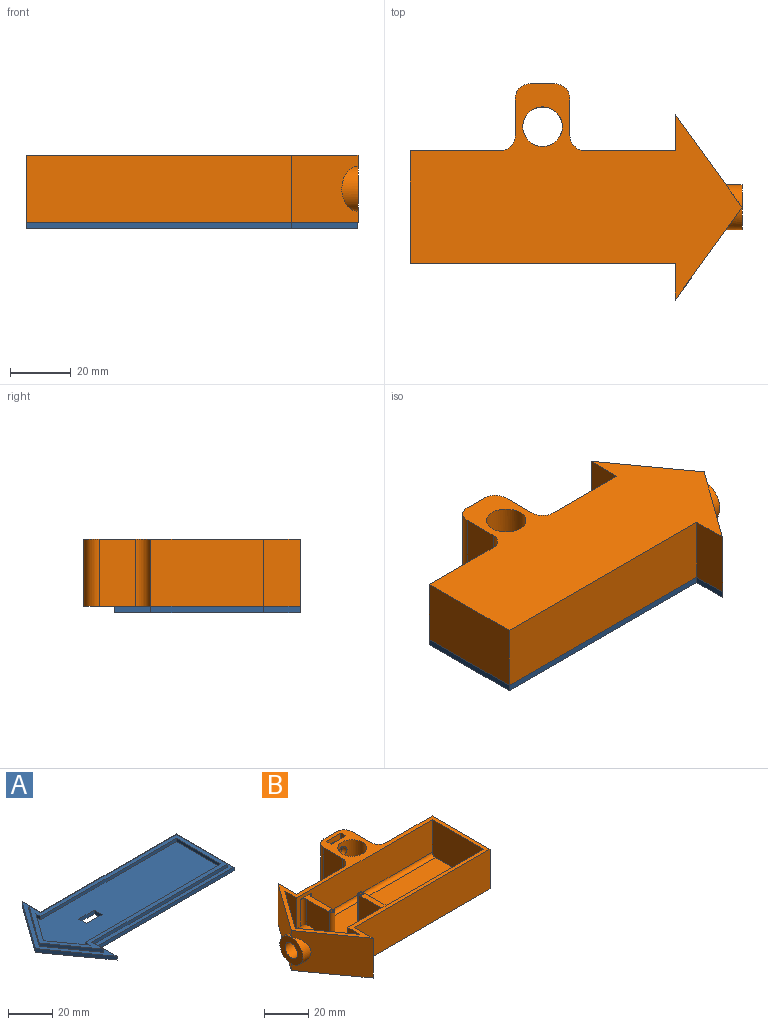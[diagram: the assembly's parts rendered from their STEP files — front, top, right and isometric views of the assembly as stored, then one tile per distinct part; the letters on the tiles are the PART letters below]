
ASSEMBLY  parts=2 mates=1
PART A: 29 faces, bbox 108.9x61x3.9 mm
  f0: plane 99.57x34.94mm, normal (0,0,1), area 2657.8mm2, adj f16,f17,f18,f19,f20,f21,f22,f25
  f1: plane 108.95x61mm, normal (0,0,-1), area 3838.3mm2, adj f2,f3,f4,f5,f6,f7,f8,f25
  f2: plane 37x2.1mm, normal (1,0,0), area 77.7mm2, adj f1,f3,f8,f9
  f3: plane 87x2.1mm, normal (0,1,0), area 182.7mm2, adj f1,f2,f4,f9
  f4: plane 12x2.1mm, normal (1,0,0), area 25.2mm2, adj f1,f3,f5,f9
  f5: plane 30.5x21.95mm, normal (-0.81,0.58,0), area 78.9mm2, adj f1,f4,f6,f9
  f6: plane 30.5x21.95mm, normal (-0.81,-0.58,0), area 78.9mm2, adj f1,f5,f7,f9
  f7: plane 12x2.1mm, normal (1,0,0), area 25.2mm2, adj f1,f6,f8,f9
  f8: plane 87x2.1mm, normal (0,-1,0), area 182.7mm2, adj f1,f2,f7,f9
  f9: plane 108.95x61mm, normal (0,0,1), area 620.8mm2, adj f2,f3,f4,f5,f6,f7,f8,f10
  f10: plane 7.59x1.8mm, normal (1,0,0), area 13.7mm2, adj f9,f11,f23,f24
  f11: plane 87x1.8mm, normal (0,-1,0), area 156.6mm2, adj f9,f10,f12,f24
  f12: plane 32.8x1.8mm, normal (1,0,0), area 59mm2, adj f9,f11,f13,f24
  f13: plane 87x1.8mm, normal (0,1,0), area 156.6mm2, adj f9,f12,f14,f24
  f14: plane 7.59x1.8mm, normal (1,0,0), area 13.7mm2, adj f9,f13,f15,f24
  f15: plane 23.99x17.26mm, normal (-0.81,0.58,0), area 53.2mm2, adj f9,f14,f23,f24
  f16: plane 87x1.8mm, normal (0,1,0), area 156.6mm2, adj f0,f17,f22,f24
  f17: plane 3.17x1.8mm, normal (-1,0,0), area 5.7mm2, adj f0,f16,f18,f24
  f18: plane 17.47x12.57mm, normal (0.81,0.58,0), area 38.7mm2, adj f0,f17,f19,f24
  f19: plane 17.47x12.57mm, normal (0.81,-0.58,0), area 38.7mm2, adj f0,f18,f20,f24
  f20: plane 3.17x1.8mm, normal (-1,0,0), area 5.7mm2, adj f0,f19,f21,f24
  f21: plane 87x1.8mm, normal (0,-1,0), area 156.6mm2, adj f0,f20,f22,f24
  f22: plane 28.6x1.8mm, normal (-1,0,0), area 51.5mm2, adj f0,f16,f21,f24
  f23: plane 23.99x17.26mm, normal (-0.81,-0.58,0), area 53.2mm2, adj f9,f10,f15,f24
  f24: plane 104.26x47.97mm, normal (0,0,1), area 559.7mm2, adj f10,f11,f12,f13,f14,f15,f16,f17
  f25: plane 5x2.1mm, normal (-1,0,0), area 10.5mm2, adj f0,f1,f26,f28
  f26: plane 10x2.1mm, normal (0,-1,0), area 21mm2, adj f0,f1,f25,f27
  f27: plane 5x2.1mm, normal (1,0,0), area 10.5mm2, adj f0,f1,f26,f28
  f28: plane 10x2.1mm, normal (0,1,0), area 21mm2, adj f0,f1,f25,f27
PART B: 65 faces, bbox 108.9x71x22.1 mm
  f0: plane 87x18mm, normal (0,-1,0), area 1454mm2, adj f2,f6,f16,f46,f59,f61,f62,f64
  f1: plane 104.26x47.97mm, normal (0,0,1), area 2839.5mm2, adj f6,f7,f8,f9,f10,f16,f49,f50
  f2: plane 108.95x71mm, normal (0,0,1), area 854.8mm2, adj f0,f3,f4,f5,f6,f7,f8,f9
  f3: plane 29.5x22.1mm, normal (0,1,0), area 652mm2, adj f2,f13,f17,f36
  f4: plane 30.5x22.1mm, normal (-0.81,0.58,0), area 725.9mm2, adj f2,f5,f13,f17,f20
  f5: plane 30.5x22.1mm, normal (-0.81,-0.58,0), area 725.9mm2, adj f2,f4,f14,f17,f19
  f6: plane 32.8x20mm, normal (-1,0,0), area 655.1mm2, adj f0,f1,f2,f7,f61
  f7: plane 87x20mm, normal (0,1,0), area 1614mm2, adj f1,f2,f6,f8,f42,f52,f55
  f8: plane 20x7.59mm, normal (-1,0,0), area 151.7mm2, adj f1,f2,f7,f9
  f9: plane 23.99x20mm, normal (0.81,0.58,0), area 486.5mm2, adj f1,f2,f8,f10,f21
  f10: plane 23.99x20mm, normal (0.81,-0.58,0), area 486.5mm2, adj f1,f2,f9,f16,f21
  f11: plane 37x22.1mm, normal (1,0,0), area 817.7mm2, adj f2,f12,f15,f17
  f12: plane 29.5x22.1mm, normal (0,1,0), area 652mm2, adj f2,f11,f17,f35
  f13: plane 22.1x12mm, normal (1,0,0), area 265.2mm2, adj f2,f3,f4,f17
  f14: plane 22.1x12mm, normal (1,0,0), area 265.2mm2, adj f2,f5,f15,f17
  f15: plane 87x22.1mm, normal (0,-1,0), area 1922.7mm2, adj f2,f11,f14,f17
  f16: plane 20x9.59mm, normal (-1,0,0), area 152.6mm2, adj f0,f1,f2,f10,f64
  f17: plane 108.95x71mm, normal (0,0,-1), area 4151.6mm2, adj f3,f4,f5,f11,f12,f13,f14,f15
  f18: plane 14.7x14.7mm, normal (-1,0,0), area 119.5mm2, adj f19,f20,f23
  f19: cylinder r=7.35mm len=14.7mm, axis (-1,0,0), area 77.7mm2, adj f5,f18
  f20: cylinder r=7.35mm len=14.7mm, axis (-1,0,0), area 77.7mm2, adj f4,f18
  f21: cylinder r=7.35mm len=14.7mm, axis (-1,0,0), area 279.2mm2, adj f9,f10,f22
  f22: plane 14.7x14.7mm, normal (1,0,0), area 119.5mm2, adj f21,f23
  f23: cylinder r=4mm len=12mm, axis (-1,0,0), area 301.6mm2, adj f18,f22
  f24: plane 22.1x12mm, normal (1,0,0), area 265.2mm2, adj f2,f17,f35,f38
  f25: plane 22.1x12mm, normal (-1,0,0), area 265.2mm2, adj f2,f17,f36,f37
  f26: plane 22.1x8mm, normal (0,1,0), area 155.2mm2, adj f2,f17,f34,f37,f38
  f27: cylinder r=6.5mm len=22.1mm, axis (0,0,1), area 880.4mm2, adj f2,f17,f33
  f28: plane 10.5x9.3mm, normal (0,-1,0), area 76mm2, adj f2,f29,f31,f32,f34
  f29: plane 10.5x3.15mm, normal (1,0,0), area 33.1mm2, adj f2,f28,f30,f32
  f30: plane 10.5x9.3mm, normal (0,1,0), area 76mm2, adj f2,f29,f31,f32,f33
  f31: plane 10.5x3.15mm, normal (-1,0,0), area 33.1mm2, adj f2,f28,f30,f32
  f32: plane 9.3x3.15mm, normal (0,0,1), area 29.3mm2, adj f28,f29,f30,f31
  f33: cylinder r=2.62mm len=5.25mm, axis (0,1,0), area 41.2mm2, adj f27,f30
  f34: cylinder r=2.62mm len=5.25mm, axis (0,1,0), area 36.7mm2, adj f26,f28
  f35: cylinder r=5mm len=22.1mm, axis (0,0,-1), area 173.6mm2, adj f2,f12,f17,f24
  f36: cylinder r=5mm len=22.1mm, axis (0,0,1), area 173.6mm2, adj f2,f3,f17,f25
  f37: cylinder r=5mm len=22.1mm, axis (0,0,-1), area 173.6mm2, adj f2,f17,f25,f26
  f38: cylinder r=5mm len=22.1mm, axis (0,0,1), area 173.6mm2, adj f2,f17,f24,f26
  f39: cylinder r=1.5mm len=16mm, axis (0,0,-1), area 75.4mm2, adj f40,f41,f42,f54
  f40: plane 16x14.4mm, normal (-1,0,0), area 230.4mm2, adj f39,f42,f52,f53
  f41: plane 16x14.4mm, normal (1,0,0), area 230.4mm2, adj f39,f42,f55,f56
  f42: plane 17.9x7mm, normal (0,0,1), area 51.7mm2, adj f7,f39,f40,f41,f47,f52,f55
  f43: plane 16x14.4mm, normal (-1,0,0), area 230.4mm2, adj f44,f46,f51,f62
  f44: cylinder r=1.5mm len=16mm, axis (0,0,-1), area 75.4mm2, adj f43,f45,f46,f50
  f45: plane 16x14.4mm, normal (1,0,0), area 230.4mm2, adj f44,f46,f49,f59
  f46: plane 17.9x7mm, normal (0,0,1), area 51.7mm2, adj f0,f43,f44,f45,f57,f59,f62
  f47: cylinder r=0.93mm len=6.35mm, axis (0,0,1), area 37.2mm2, adj f42,f48
  f48: plane 1.87x1.87mm, normal (0,0,1), area 2.7mm2, adj f47
  f49: cylinder r=2mm len=14.4mm, axis (0,-1,0), area 45.2mm2, adj f1,f45,f50,f60
  f50: torus R=3.5mm, axis (0,0,-1), area 22mm2, adj f1,f44,f49,f51
  f51: cylinder r=2mm len=14.4mm, axis (0,1,0), area 45.2mm2, adj f1,f43,f50,f63
  f52: cylinder r=2mm len=18mm, axis (0,0,-1), area 54.3mm2, adj f7,f40,f42,f53
  f53: cylinder r=2mm len=16.4mm, axis (0,1,0), area 49.2mm2, adj f1,f40,f52,f54
  f54: torus R=3.5mm, axis (0,0,-1), area 22mm2, adj f1,f39,f53,f56
  f55: cylinder r=2mm len=18mm, axis (0,0,1), area 54.3mm2, adj f7,f41,f42,f56
  f56: cylinder r=2mm len=16.4mm, axis (0,-1,0), area 49.2mm2, adj f1,f41,f54,f55
  f57: cylinder r=0.93mm len=6.35mm, axis (0,0,1), area 37.2mm2, adj f46,f58
  f58: plane 1.87x1.87mm, normal (0,0,1), area 2.7mm2, adj f57
  f59: cylinder r=2mm len=16mm, axis (0,0,1), area 50.3mm2, adj f0,f45,f46,f60
  f60: sphere r=2mm, area 6.3mm2, adj f49,f59,f61
  f61: cylinder r=2mm len=77.55mm, axis (-1,0,0), area 243.6mm2, adj f0,f1,f6,f60
  f62: cylinder r=2mm len=16mm, axis (0,0,-1), area 50.3mm2, adj f0,f43,f46,f63
  f63: sphere r=2mm, area 6.3mm2, adj f51,f62,f64
  f64: cylinder r=2mm len=2.45mm, axis (-1,0,0), area 7.7mm2, adj f0,f1,f16,f63
PLACE A rot(axis=(0,0,1),180deg) t=(33.44,49.9,-7.92)mm
PLACE B rot(axis=(0,1,0),180deg) t=(6.67,62.31,14.18)mm fixed
MATE fastened B.f2 <-> A.f9  axis (0,0,-1) through (80.79,49.9,-5.82)mm
